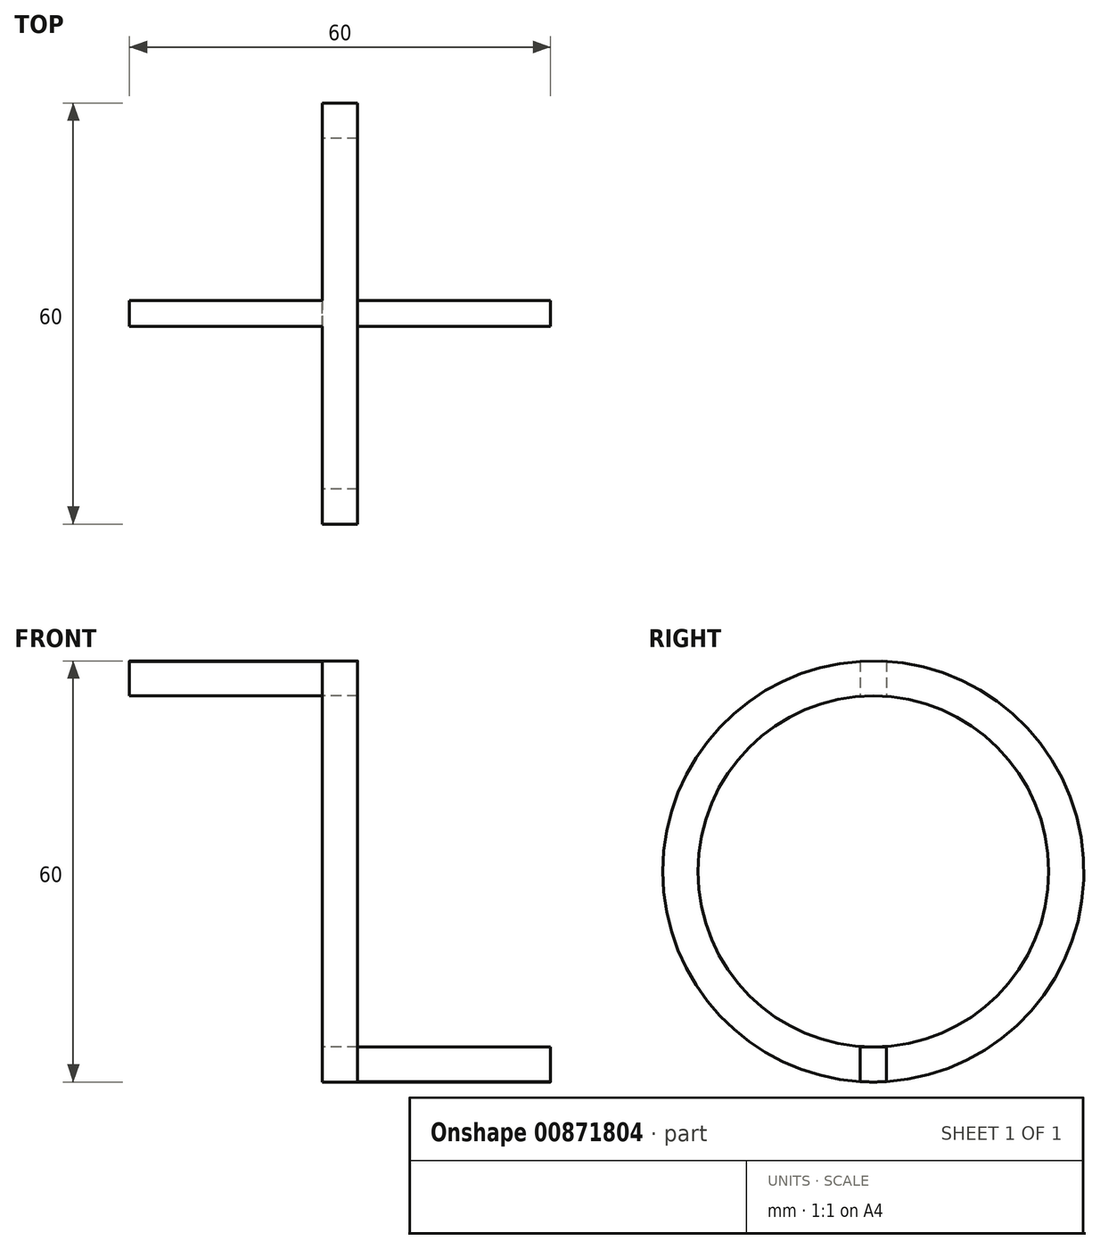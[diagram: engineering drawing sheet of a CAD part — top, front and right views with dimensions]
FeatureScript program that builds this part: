
annotation { "Feature Type Name" : "Feature", "Feature Type Description" : "" }
export const myFeature = defineFeature(function(context is Context, id is Id, definition is map)
    precondition{}
    {
        {
            var Q0;
            Q0=qCreatedBy(makeId("Right.planeOp"),FACE);
            var sketch = newSketch(context, id + "F0", { "sketchPlane" : qUnion([Q0])});
            skCircle(sketch, "E0", {"center": v(0, 0) * mm, "radius": 30 * mm});
            skCircle(sketch, "E1", {"center": v(0, 0) * mm, "radius": 25 * mm});
            skSolve(sketch);
        }
        {
            var Q0;
            Q0 = qSketchRegion(id + "F0", true);
            extrude(context, id + "F1", {"entities" : qUnion([Q0]), "depth" : 60 * mm, "offsetDistance" : 25 * mm});
        }
        {
            var Q0;
            Q0=qCreatedBy(makeId("Front.planeOp"),FACE);
            var sketch = newSketch(context, id + "F2", { "sketchPlane" : qUnion([Q0])});
            skLineSegment(sketch, "E2", {"start": v(0, 30) * mm, "end": v(32.5, 30) * mm});
            skLineSegment(sketch, "E3", {"start": v(32.5, 30) * mm, "end": v(32.5, -25) * mm});
            skLineSegment(sketch, "E4", {"start": v(32.5, -25) * mm, "end": v(60, -25) * mm});
            skLineSegment(sketch, "E5", {"start": v(60, -25) * mm, "end": v(60, -30) * mm});
            skLineSegment(sketch, "E6", {"start": v(60, -30) * mm, "end": v(27.5, -30) * mm});
            skLineSegment(sketch, "E7", {"start": v(27.5, -30) * mm, "end": v(27.5, 25) * mm});
            skLineSegment(sketch, "E8", {"start": v(27.5, 25) * mm, "end": v(0, 25) * mm});
            skLineSegment(sketch, "E9", {"start": v(0, 25) * mm, "end": v(0, 30) * mm});
            skLineSegment(sketch, "E10", {"start": v(30, 44.82) * mm, "end": v(30, 9.84) * mm, "construction": true});
            skSolve(sketch);
        }
        {
            var Q0;
            Q0 = qSketchRegion(id + "F2", true);
            extrude(context, id + "F3", {"entities" : qUnion([Q0]), "depth" : 80 * mm, "offsetDistance" : 25 * mm, "symmetric" : true});
        }
        {
            var Q0;
            Q0=makeQuery(id+"F3.opExtrude","SWEPT_BODY",BODY,{"disambiguationData":[OSD([sQuery(id+"F2.wireOp",EDGE,"E2"),sQuery(id+"F2.wireOp",EDGE,"E3"),sQuery(id+"F2.wireOp",EDGE,"E4"),sQuery(id+"F2.wireOp",EDGE,"E5"),sQuery(id+"F2.wireOp",EDGE,"E6"),sQuery(id+"F2.wireOp",EDGE,"E7"),sQuery(id+"F2.wireOp",EDGE,"E8"),sQuery(id+"F2.wireOp",EDGE,"E9")])]});
            var Q1;
            Q1=makeQuery(id+"F1.opExtrude","SWEPT_BODY",BODY,{"disambiguationData":[OSD([sQuery(id+"F0.wireOp",EDGE,"E0"),sQuery(id+"F0.wireOp",EDGE,"E1")])]});
            booleanBodies(context, id + "F4", {"operationType" : BooleanOperationType.INTERSECTION, "tools" : qUnion([Q0, Q1])});
        }
        {
            var Q0;
            Q0=qCreatedBy(makeId("Top.planeOp"),FACE);
            var sketch = newSketch(context, id + "F5", { "sketchPlane" : qUnion([Q0])});
            skLineSegment(sketch, "E11", {"start": v(0, 1.85) * mm, "end": v(27.5, 1.85) * mm});
            skLineSegment(sketch, "E12", {"start": v(27.5, 1.85) * mm, "end": v(27.5, 30) * mm});
            skLineSegment(sketch, "E13", {"start": v(27.5, 30) * mm, "end": v(32.5, 30) * mm});
            skLineSegment(sketch, "E14", {"start": v(32.5, 30) * mm, "end": v(32.5, 1.85) * mm});
            skLineSegment(sketch, "E15", {"start": v(32.5, 1.85) * mm, "end": v(60, 1.85) * mm});
            skLineSegment(sketch, "E16", {"start": v(60, 1.85) * mm, "end": v(60, -1.85) * mm});
            skLineSegment(sketch, "E17", {"start": v(60, -1.85) * mm, "end": v(32.5, -1.85) * mm});
            skLineSegment(sketch, "E18", {"start": v(32.5, -1.85) * mm, "end": v(32.5, -30) * mm});
            skLineSegment(sketch, "E19", {"start": v(32.5, -30) * mm, "end": v(27.5, -30) * mm});
            skLineSegment(sketch, "E20", {"start": v(27.5, -30) * mm, "end": v(27.5, -1.85) * mm});
            skLineSegment(sketch, "E21", {"start": v(27.5, -1.85) * mm, "end": v(0, -1.85) * mm});
            skLineSegment(sketch, "E22", {"start": v(0, -1.85) * mm, "end": v(0, 1.85) * mm});
            skLineSegment(sketch, "E23", {"start": v(0, 0) * mm, "end": v(2.29, 0) * mm, "construction": true});
            skSolve(sketch);
        }
        {
            var Q0;
            Q0 = qSketchRegion(id + "F5", true);
            extrude(context, id + "F6", {"entities" : qUnion([Q0]), "depth" : 80 * mm, "offsetDistance" : 25 * mm, "symmetric" : true});
        }
        {
            var Q0;
            Q0=makeQuery(id+"F6.opExtrude","SWEPT_BODY",BODY,{"disambiguationData":[OSD([sQuery(id+"F5.wireOp",EDGE,"E11"),sQuery(id+"F5.wireOp",EDGE,"E12"),sQuery(id+"F5.wireOp",EDGE,"E13"),sQuery(id+"F5.wireOp",EDGE,"E14"),sQuery(id+"F5.wireOp",EDGE,"E15"),sQuery(id+"F5.wireOp",EDGE,"E16"),sQuery(id+"F5.wireOp",EDGE,"E17"),sQuery(id+"F5.wireOp",EDGE,"E18"),sQuery(id+"F5.wireOp",EDGE,"E19"),sQuery(id+"F5.wireOp",EDGE,"E20"),sQuery(id+"F5.wireOp",EDGE,"E21"),sQuery(id+"F5.wireOp",EDGE,"E22")])]});
            var Q1;
            Q1=makeQuery(id+"F4.opBoolean","INTERSECT",BODY,{"derivedFrom":[makeQuery(id+"F1.opExtrude","SWEPT_BODY",BODY,{"disambiguationData":[OSD([sQuery(id+"F0.wireOp",EDGE,"E0"),sQuery(id+"F0.wireOp",EDGE,"E1")])]}),makeQuery(id+"F3.opExtrude","SWEPT_BODY",BODY,{"disambiguationData":[OSD([sQuery(id+"F2.wireOp",EDGE,"E2"),sQuery(id+"F2.wireOp",EDGE,"E3"),sQuery(id+"F2.wireOp",EDGE,"E4"),sQuery(id+"F2.wireOp",EDGE,"E5"),sQuery(id+"F2.wireOp",EDGE,"E6"),sQuery(id+"F2.wireOp",EDGE,"E7"),sQuery(id+"F2.wireOp",EDGE,"E8"),sQuery(id+"F2.wireOp",EDGE,"E9")])]})]});
            booleanBodies(context, id + "F7", {"operationType" : BooleanOperationType.INTERSECTION, "tools" : qUnion([Q0, Q1])});
        }
    });
